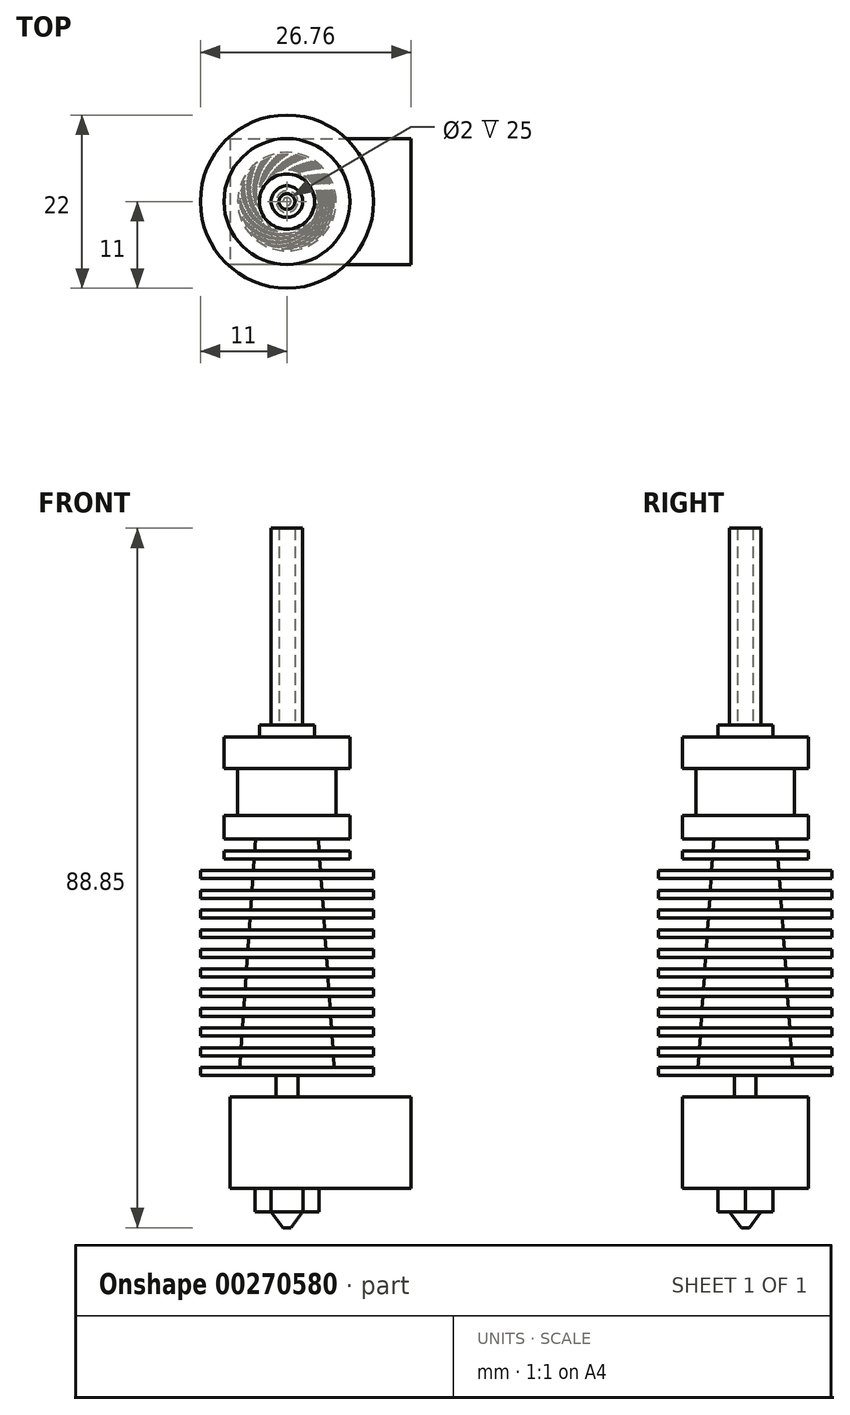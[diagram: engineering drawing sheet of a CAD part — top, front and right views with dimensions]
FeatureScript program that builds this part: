
annotation { "Feature Type Name" : "Feature", "Feature Type Description" : "" }
export const myFeature = defineFeature(function(context is Context, id is Id, definition is map)
    precondition{}
    {
        {
            var Q0;
            Q0=qCreatedBy(makeId("Right.planeOp"),FACE);
            var sketch = newSketch(context, id + "F0", { "sketchPlane" : qUnion([Q0])});
            skLineSegment(sketch, "E0", {"start": v(0, 0) * mm, "end": v(0.5, 0) * mm});
            skLineSegment(sketch, "E1", {"start": v(0, 2) * mm, "end": v(2, 2) * mm});
            skLineSegment(sketch, "E2", {"start": v(0, 2) * mm, "end": v(0, 0) * mm});
            skLineSegment(sketch, "E3", {"start": v(0.5, 0) * mm, "end": v(2, 2) * mm});
            skSolve(sketch);
        }
        {
            var Q0;
            Q0 = qSketchRegion(id + "F0", true);
            var Q1;
            Q1=sQuery(id+"F0.wireOp",EDGE,"E2");
            revolve(context, id + "F1", {"entities" : qUnion([Q0]), "axis" : qUnion([Q1]), "revolveType" : RevolveType.FULL});
        }
        {
            var Q0;
            Q0=makeQuery(id+"F1.opRevolve","SWEPT_FACE",FACE,{"disambiguationData":[OSD([sQuery(id+"F0.wireOp",EDGE,"E1")])]});
            var sketch = newSketch(context, id + "F2", { "sketchPlane" : qUnion([Q0])});
            skLineSegment(sketch, "E4", {"start": v(-2.02, 3.5) * mm, "end": v(2.02, 3.5) * mm});
            skLineSegment(sketch, "E5", {"start": v(-2.02, -3.5) * mm, "end": v(2.02, -3.5) * mm});
            skLineSegment(sketch, "E6", {"start": v(-2.02, 3.5) * mm, "end": v(-4.04, 0) * mm});
            skLineSegment(sketch, "E7", {"start": v(-4.04, 0) * mm, "end": v(-2.02, -3.5) * mm});
            skLineSegment(sketch, "E8", {"start": v(2.02, -3.5) * mm, "end": v(4.04, 0) * mm});
            skLineSegment(sketch, "E9", {"start": v(4.04, 0) * mm, "end": v(2.02, 3.5) * mm});
            skLineSegment(sketch, "E10", {"start": v(4.04, 4.39) * mm, "end": v(4.04, -4.08) * mm, "construction": true});
            skLineSegment(sketch, "E11", {"start": v(-4.04, 3.84) * mm, "end": v(-4.04, -4.08) * mm, "construction": true});
            skSolve(sketch);
        }
        {
            var Q0;
            Q0 = qSketchRegion(id + "F2", true);
            extrude(context, id + "F3", {"entities" : qUnion([Q0]), "operationType" : NewBodyOperationType.ADD, "depth" : 3 * mm});
        }
        {
            var Q0;
            Q0=makeQuery(id+"F3.opExtrude","CAP_FACE",FACE,{"disambiguationData":[OSD([sQuery(id+"F2.wireOp",EDGE,"E4"),sQuery(id+"F2.wireOp",EDGE,"E5"),sQuery(id+"F2.wireOp",EDGE,"E6"),sQuery(id+"F2.wireOp",EDGE,"E7"),sQuery(id+"F2.wireOp",EDGE,"E8"),sQuery(id+"F2.wireOp",EDGE,"E9")])],"isStart":false});
            var sketch = newSketch(context, id + "F4", { "sketchPlane" : qUnion([Q0])});
            skLineSegment(sketch, "E12", {"start": v(-4.04, 7.54) * mm, "end": v(-4.04, -6.8) * mm, "construction": true});
            skLineSegment(sketch, "E13", {"start": v(-7.24, 8) * mm, "end": v(-7.24, -8) * mm});
            skLineSegment(sketch, "E14", {"start": v(-7.24, 8) * mm, "end": v(15.76, 8) * mm});
            skLineSegment(sketch, "E15", {"start": v(15.76, 8) * mm, "end": v(15.76, -8) * mm});
            skLineSegment(sketch, "E16", {"start": v(15.76, -8) * mm, "end": v(-7.24, -8) * mm});
            skSolve(sketch);
        }
        {
            var Q0;
            Q0 = qSketchRegion(id + "F4", true);
            extrude(context, id + "F5", {"entities" : qUnion([Q0]), "operationType" : NewBodyOperationType.ADD, "depth" : 11.6 * mm});
        }
        {
            var Q0;
            Q0=makeQuery(id+"F5.opExtrude","CAP_FACE",FACE,{"disambiguationData":[OSD([sQuery(id+"F4.wireOp",EDGE,"E13"),sQuery(id+"F4.wireOp",EDGE,"E14"),sQuery(id+"F4.wireOp",EDGE,"E15"),sQuery(id+"F4.wireOp",EDGE,"E16")])],"isStart":false});
            var sketch = newSketch(context, id + "F6", { "sketchPlane" : qUnion([Q0])});
            skCircle(sketch, "E17.0", {"center": v(0, 0) * mm, "radius": 2 * mm, "construction": true});
            skCircle(sketch, "E18", {"center": v(0, 0) * mm, "radius": 1.38 * mm});
            skSolve(sketch);
        }
        {
            var Q0;
            Q0 = qSketchRegion(id + "F6", true);
            extrude(context, id + "F7", {"entities" : qUnion([Q0]), "operationType" : NewBodyOperationType.ADD, "depth" : 2.75 * mm});
        }
        {
            var Q0;
            Q0=qCreatedBy(makeId("Front.planeOp"),FACE);
            var sketch = newSketch(context, id + "F8", { "sketchPlane" : qUnion([Q0])});
            skLineSegment(sketch, "E19", {"start": v(0, 18.7) * mm, "end": v(0, 62.35) * mm});
            skLineSegment(sketch, "E20.0", {"start": v(-1.38, 19.35) * mm, "end": v(0, 19.35) * mm, "construction": true});
            skLineSegment(sketch, "E21", {"start": v(1.38, 19.35) * mm, "end": v(11, 19.35) * mm});
            skLineSegment(sketch, "E22", {"start": v(11, 19.35) * mm, "end": v(11, 20.35) * mm});
            skLineSegment(sketch, "E23", {"start": v(11, 20.35) * mm, "end": v(6, 20.35) * mm});
            skLineSegment(sketch, "E24", {"start": v(1.38, 19.35) * mm, "end": v(1.38, 20.35) * mm, "construction": true});
            skLineSegment(sketch, "E25", {"start": v(1.37, 20.35) * mm, "end": v(1.37, 21.85) * mm, "construction": true});
            skLineSegment(sketch, "E26", {"start": v(1.38, 19.35) * mm, "end": v(0, 19.35) * mm});
            skLineSegment(sketch, "E27.0.1.0", {"start": v(5.9, 21.85) * mm, "end": v(11, 21.85) * mm});
            skLineSegment(sketch, "E27.0.1.1", {"start": v(11, 21.85) * mm, "end": v(11, 22.85) * mm});
            skLineSegment(sketch, "E27.0.1.2", {"start": v(11, 22.85) * mm, "end": v(5.83, 22.85) * mm});
            skLineSegment(sketch, "E27.0.2.0", {"start": v(5.72, 24.35) * mm, "end": v(11, 24.35) * mm});
            skLineSegment(sketch, "E27.0.2.1", {"start": v(11, 24.35) * mm, "end": v(11, 25.35) * mm});
            skLineSegment(sketch, "E27.0.2.2", {"start": v(11, 25.35) * mm, "end": v(5.65, 25.35) * mm});
            skLineSegment(sketch, "E27.0.3.0", {"start": v(5.55, 26.85) * mm, "end": v(11, 26.85) * mm});
            skLineSegment(sketch, "E27.0.3.1", {"start": v(11, 26.85) * mm, "end": v(11, 27.85) * mm});
            skLineSegment(sketch, "E27.0.3.2", {"start": v(11, 27.85) * mm, "end": v(5.48, 27.85) * mm});
            skLineSegment(sketch, "E27.0.4.0", {"start": v(5.38, 29.35) * mm, "end": v(11, 29.35) * mm});
            skLineSegment(sketch, "E27.0.4.1", {"start": v(11, 29.35) * mm, "end": v(11, 30.35) * mm});
            skLineSegment(sketch, "E27.0.4.2", {"start": v(11, 30.35) * mm, "end": v(5.3, 30.35) * mm});
            skLineSegment(sketch, "E27.0.5.0", {"start": v(5.2, 31.85) * mm, "end": v(11, 31.85) * mm});
            skLineSegment(sketch, "E27.0.5.1", {"start": v(11, 31.85) * mm, "end": v(11, 32.85) * mm});
            skLineSegment(sketch, "E27.0.5.2", {"start": v(11, 32.85) * mm, "end": v(5.14, 32.85) * mm});
            skLineSegment(sketch, "E27.0.6.0", {"start": v(5.03, 34.35) * mm, "end": v(11, 34.35) * mm});
            skLineSegment(sketch, "E27.0.6.1", {"start": v(11, 34.35) * mm, "end": v(11, 35.35) * mm});
            skLineSegment(sketch, "E27.0.6.2", {"start": v(11, 35.35) * mm, "end": v(4.96, 35.35) * mm});
            skLineSegment(sketch, "E27.0.7.0", {"start": v(4.86, 36.85) * mm, "end": v(11, 36.85) * mm});
            skLineSegment(sketch, "E27.0.7.1", {"start": v(11, 36.85) * mm, "end": v(11, 37.85) * mm});
            skLineSegment(sketch, "E27.0.7.2", {"start": v(11, 37.85) * mm, "end": v(4.79, 37.85) * mm});
            skLineSegment(sketch, "E27.0.8.0", {"start": v(4.69, 39.35) * mm, "end": v(11, 39.35) * mm});
            skLineSegment(sketch, "E27.0.8.1", {"start": v(11, 39.35) * mm, "end": v(11, 40.35) * mm});
            skLineSegment(sketch, "E27.0.8.2", {"start": v(11, 40.35) * mm, "end": v(4.62, 40.35) * mm});
            skLineSegment(sketch, "E27.0.9.0", {"start": v(4.51, 41.85) * mm, "end": v(11, 41.85) * mm});
            skLineSegment(sketch, "E27.0.9.1", {"start": v(11, 41.85) * mm, "end": v(11, 42.85) * mm});
            skLineSegment(sketch, "E27.0.9.2", {"start": v(11, 42.85) * mm, "end": v(4.44, 42.85) * mm});
            skLineSegment(sketch, "E27.direction1", {"start": v(1.37, 19.35) * mm, "end": v(26.38, 19.35) * mm, "construction": true});
            skLineSegment(sketch, "E28", {"start": v(4.34, 44.35) * mm, "end": v(11, 44.35) * mm});
            skLineSegment(sketch, "E29", {"start": v(11, 44.35) * mm, "end": v(11, 45.35) * mm});
            skLineSegment(sketch, "E30", {"start": v(11, 45.35) * mm, "end": v(4.27, 45.35) * mm});
            skLineSegment(sketch, "E31", {"start": v(6, 20.35) * mm, "end": v(5.9, 21.85) * mm});
            skPoint(sketch, "E32.orphan", {"position": v(1.38, 21.85) * mm});
            skPoint(sketch, "E33.orphan", {"position": v(1.38, 24.35) * mm});
            skLineSegment(sketch, "E34.trimOffspring", {"start": v(5.83, 22.85) * mm, "end": v(5.72, 24.35) * mm});
            skLineSegment(sketch, "E35.trimOffspring", {"start": v(5.65, 25.35) * mm, "end": v(5.55, 26.85) * mm});
            skPoint(sketch, "E36.orphan", {"position": v(1.38, 26.85) * mm});
            skLineSegment(sketch, "E37.trimOffspring", {"start": v(5.48, 27.85) * mm, "end": v(5.38, 29.35) * mm});
            skPoint(sketch, "E38.orphan", {"position": v(1.38, 29.35) * mm});
            skPoint(sketch, "E39.orphan", {"position": v(1.38, 31.85) * mm});
            skPoint(sketch, "E40.orphan", {"position": v(1.38, 34.35) * mm});
            skPoint(sketch, "E41.orphan", {"position": v(1.38, 36.85) * mm});
            skPoint(sketch, "E42.orphan", {"position": v(1.38, 39.35) * mm});
            skPoint(sketch, "E43.orphan", {"position": v(1.38, 41.85) * mm});
            skLineSegment(sketch, "E44.trimOffspring", {"start": v(4.44, 42.85) * mm, "end": v(4.34, 44.35) * mm});
            skLineSegment(sketch, "E45.trimOffspring", {"start": v(4.62, 40.35) * mm, "end": v(4.51, 41.85) * mm});
            skLineSegment(sketch, "E46.trimOffspring", {"start": v(4.79, 37.85) * mm, "end": v(4.69, 39.35) * mm});
            skLineSegment(sketch, "E47.trimOffspring", {"start": v(4.96, 35.35) * mm, "end": v(4.86, 36.85) * mm});
            skLineSegment(sketch, "E48.trimOffspring", {"start": v(5.14, 32.85) * mm, "end": v(5.03, 34.35) * mm});
            skLineSegment(sketch, "E49.trimOffspring", {"start": v(5.3, 30.35) * mm, "end": v(5.2, 31.85) * mm});
            skLineSegment(sketch, "E50", {"start": v(4.27, 45.35) * mm, "end": v(4.17, 46.85) * mm});
            skLineSegment(sketch, "E51", {"start": v(0, 45.35) * mm, "end": v(0, 46.85) * mm});
            skLineSegment(sketch, "E52", {"start": v(4.17, 46.85) * mm, "end": v(8, 46.85) * mm});
            skLineSegment(sketch, "E53", {"start": v(8, 46.85) * mm, "end": v(8, 47.85) * mm});
            skLineSegment(sketch, "E54", {"start": v(8, 47.85) * mm, "end": v(4.1, 47.85) * mm});
            skLineSegment(sketch, "E55", {"start": v(4, 49.35) * mm, "end": v(8, 49.35) * mm});
            skLineSegment(sketch, "E56", {"start": v(8, 49.35) * mm, "end": v(8, 52.35) * mm});
            skLineSegment(sketch, "E57", {"start": v(8, 52.35) * mm, "end": v(6.25, 52.35) * mm});
            skLineSegment(sketch, "E58.trimOffspring", {"start": v(4.1, 47.85) * mm, "end": v(4, 49.35) * mm});
            skLineSegment(sketch, "E59", {"start": v(6.25, 52.35) * mm, "end": v(6.25, 58.35) * mm});
            skLineSegment(sketch, "E60", {"start": v(6.25, 58.35) * mm, "end": v(8, 58.35) * mm});
            skLineSegment(sketch, "E61", {"start": v(8, 58.35) * mm, "end": v(8, 62.35) * mm});
            skLineSegment(sketch, "E62", {"start": v(8, 62.35) * mm, "end": v(0, 62.35) * mm});
            skSolve(sketch);
        }
        {
            var Q0;
            Q0 = qSketchRegion(id + "F8", true);
            var Q1;
            Q1=sQuery(id+"F8.wireOp",EDGE,"E19");
            revolve(context, id + "F9", {"operationType" : NewBodyOperationType.ADD, "entities" : qUnion([Q0]), "axis" : qUnion([Q1]), "revolveType" : RevolveType.FULL});
        }
        {
            var Q0;
            Q0=makeQuery(id+"F9.opRevolve","SWEPT_FACE",FACE,{"disambiguationData":[OSD([sQuery(id+"F8.wireOp",EDGE,"E62")])]});
            var sketch = newSketch(context, id + "F10", { "sketchPlane" : qUnion([Q0])});
            skCircle(sketch, "E63.0", {"center": v(0, 0) * mm, "radius": 8 * mm, "construction": true});
            skCircle(sketch, "E64", {"center": v(0, 0) * mm, "radius": 3.5 * mm});
            skSolve(sketch);
        }
        {
            var Q0;
            Q0 = qSketchRegion(id + "F10", true);
            extrude(context, id + "F11", {"entities" : qUnion([Q0]), "operationType" : NewBodyOperationType.ADD, "depth" : 1.5 * mm});
        }
        {
            var Q0;
            Q0=makeQuery(id+"F11.opExtrude","CAP_FACE",FACE,{"disambiguationData":[OSD([sQuery(id+"F10.wireOp",EDGE,"E64")])],"isStart":false});
            var sketch = newSketch(context, id + "F12", { "sketchPlane" : qUnion([Q0])});
            skCircle(sketch, "E65.0", {"center": v(0, 0) * mm, "radius": 3.5 * mm, "construction": true});
            skCircle(sketch, "E66", {"center": v(0, 0) * mm, "radius": 2 * mm});
            skCircle(sketch, "E67", {"center": v(0, 0) * mm, "radius": 1 * mm});
            skSolve(sketch);
        }
        {
            var Q0;
            Q0 = qSketchRegion(id + "F12", true);
            extrude(context, id + "F13", {"entities" : qUnion([Q0]), "operationType" : NewBodyOperationType.ADD, "depth" : 25 * mm});
        }
    });
